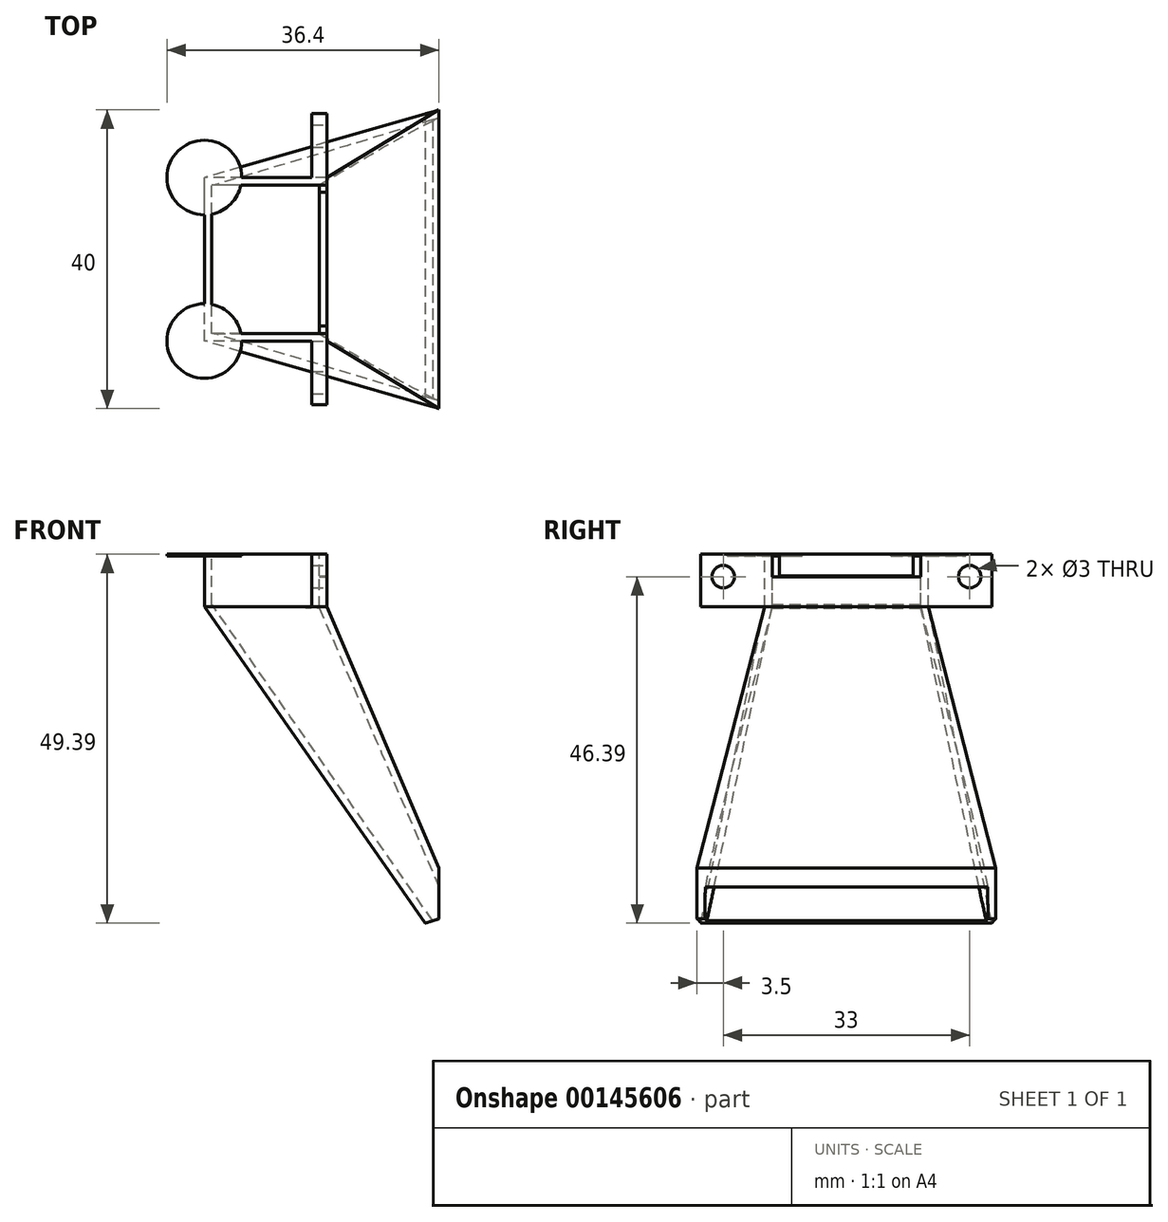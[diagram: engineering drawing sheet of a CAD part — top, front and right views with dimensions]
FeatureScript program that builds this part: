
annotation { "Feature Type Name" : "Feature", "Feature Type Description" : "" }
export const myFeature = defineFeature(function(context is Context, id is Id, definition is map)
    precondition{}
    {
        {
            assignVariable(context, id + "F0", {"name" : "fan_wide", "anyValue" : 19.9});
        }
        {
            assignVariable(context, id + "F1", {"name" : "shell", "anyValue" : 1});
        }
        {
            var Q0;
            Q0=qCreatedBy(makeId("Front.planeOp"),FACE);
            var sketch = newSketch(context, id + "F2", { "sketchPlane" : qUnion([Q0])});
            skLineSegment(sketch, "E0.bottom", {"start": v(0, 0) * mm, "end": v(-16.4, 0) * mm});
            skLineSegment(sketch, "E0.top", {"start": v(0, 7) * mm, "end": v(-16.4, 7) * mm});
            skLineSegment(sketch, "E0.left", {"start": v(0, 0) * mm, "end": v(0, 7) * mm});
            skLineSegment(sketch, "E0.right", {"start": v(-16.4, 0) * mm, "end": v(-16.4, 7) * mm});
            skLineSegment(sketch, "E1", {"start": v(-16.4, 0) * mm, "end": v(15, -45) * mm});
            skLineSegment(sketch, "E2", {"start": v(15, -45) * mm, "end": v(15, -35) * mm});
            skLineSegment(sketch, "E3", {"start": v(15, -35) * mm, "end": v(0, 0) * mm});
            skSolve(sketch);
        }
        {
            var Q0;
            Q0=makeQuery(id+"F2.imprint","IMPRINT",FACE,{"disambiguationData":[TD([[makeQuery(id+"F2.imprint","IMPRINT",EDGE,{"derivedFrom":sQuery(id+"F2.wireOp",EDGE,"E0.bottom")}),-1.0]])]});
            var Q1;
            Q1=makeQuery(id+"F2.imprint","IMPRINT",FACE,{"disambiguationData":[TD([[makeQuery(id+"F2.imprint","IMPRINT",EDGE,{"derivedFrom":sQuery(id+"F2.wireOp",EDGE,"E0.bottom")}),1.0]])]});
            extrude(context, id + "F3", {"entities" : qUnion([Q0, Q1]), "depth" : (getVariable(context, 'fan_wide') + 2 * getVariable(context, 'shell')) * mm, "offsetDistance" : 25 * mm});
        }
        {
            var Q0;
            Q0=qCreatedBy(makeId("Top.planeOp"),FACE);
            var sketch = newSketch(context, id + "F4", { "sketchPlane" : qUnion([Q0])});
            skLineSegment(sketch, "E4.0.0", {"start": v(0, 0) * mm, "end": v(-16.4, 0) * mm});
            skLineSegment(sketch, "E4.0.1", {"start": v(-16.4, 0) * mm, "end": v(-16.4, -21.9) * mm});
            skLineSegment(sketch, "E4.0.2", {"start": v(-16.4, -21.9) * mm, "end": v(0, -21.9) * mm});
            skLineSegment(sketch, "E4.0.3", {"start": v(0, -21.9) * mm, "end": v(0, 0) * mm});
            skSolve(sketch);
        }
        {
            var Q0;
            Q0=makeQuery(id+"F3.opExtrude","SWEPT_FACE",FACE,{"disambiguationData":[OSD([sQuery(id+"F2.wireOp",EDGE,"E2")])]});
            cPlane(context, id + "F5", {"entities" : qUnion([Q0]), "cplaneType" : CPlaneType.OFFSET, "offset" : 0 * mm, "width" : 150 * mm, "height" : 150 * mm});
        }
        {
            var Q0;
            Q0=qCreatedBy(id+"F5.planeOp",FACE);
            var sketch = newSketch(context, id + "F6", { "sketchPlane" : qUnion([Q0])});
            skLineSegment(sketch, "E5.0.0", {"start": v(0, -45) * mm, "end": v(0, -35) * mm, "construction": true});
            skLineSegment(sketch, "E5.0.1", {"start": v(0, -35) * mm, "end": v(-21.9, -35) * mm, "construction": true});
            skLineSegment(sketch, "E5.0.2", {"start": v(-21.9, -35) * mm, "end": v(-21.9, -45) * mm, "construction": true});
            skLineSegment(sketch, "E5.0.3", {"start": v(-21.9, -45) * mm, "end": v(0, -45) * mm, "construction": true});
            skLineSegment(sketch, "E6", {"start": v(-21.9, -35) * mm, "end": v(0, -45) * mm, "construction": true});
            skPoint(sketch, "E7", {"position": v(-10.95, -40) * mm});
            skLineSegment(sketch, "E8.bottom", {"start": v(9.05, -35) * mm, "end": v(-30.95, -35) * mm});
            skLineSegment(sketch, "E8.top", {"start": v(9.05, -45) * mm, "end": v(-30.95, -45) * mm});
            skLineSegment(sketch, "E8.left", {"start": v(9.05, -35) * mm, "end": v(9.05, -45) * mm});
            skLineSegment(sketch, "E8.right", {"start": v(-30.95, -35) * mm, "end": v(-30.95, -45) * mm});
            skSolve(sketch);
        }
        {
            var Q1;
            Q1=makeQuery(id+"F6.imprint","IMPRINT",FACE,{"disambiguationData":[TD([[makeQuery(id+"F6.imprint","IMPRINT",EDGE,{"derivedFrom":sQuery(id+"F6.wireOp",EDGE,"E8.bottom")}),1.0]])]});
            var Q2;
            Q2=makeQuery(id+"F4.imprint","IMPRINT",FACE,{"disambiguationData":[TD([[makeQuery(id+"F4.imprint","IMPRINT",EDGE,{"derivedFrom":sQuery(id+"F4.wireOp",EDGE,"E4.0.0")}),1.0]])]});
            loft(context, id + "F7", {"operationType" : NewBodyOperationType.ADD, "sheetProfilesArray" : [{ "sheetProfileEntities" : qUnion([Q1]) }, { "sheetProfileEntities" : qUnion([Q2]) }]});
        }
        {
            var Q0;
            Q0=makeQuery(id+"F3.opExtrude","SWEPT_FACE",FACE,{"disambiguationData":[OSD([sQuery(id+"F2.wireOp",EDGE,"E0.top")])]});
            var Q1;
            Q1=makeQuery(id+"F7.boolean.opBoolean","MERGE",FACE,{"derivedFrom":[makeQuery(id+"F3.opExtrude","SWEPT_FACE",FACE,{"disambiguationData":[OSD([sQuery(id+"F2.wireOp",EDGE,"E2")])]}),makeQuery(id+"F7.opLoft","CAP_FACE",FACE,{"disambiguationData":[OSD([makeQuery(id+"F6.imprint","IMPRINT",FACE,{"disambiguationData":[TD([[makeQuery(id+"F6.imprint","IMPRINT",EDGE,{"derivedFrom":sQuery(id+"F6.wireOp",EDGE,"E8.bottom")}),1.0]])]})])],"isStart":true})]});
            shell(context, id + "F8", {"entities" : qUnion([Q0, Q1]), "thickness" : (getVariable(context, 'shell')) * mm});
        }
        {
            var Q0;
            Q0=makeQuery(id+"F3.opExtrude","SWEPT_FACE",FACE,{"disambiguationData":[OSD([sQuery(id+"F2.wireOp",EDGE,"E0.left")])]});
            var sketch = newSketch(context, id + "F9", { "sketchPlane" : qUnion([Q0])});
            skLineSegment(sketch, "E9", {"start": v(-10.95, 7) * mm, "end": v(-10.95, 0) * mm, "construction": true});
            skLineSegment(sketch, "E10", {"start": v(-27.45, 4) * mm, "end": v(5.55, 4) * mm, "construction": true});
            skCircle(sketch, "E11", {"center": v(-27.45, 4) * mm, "radius": 1.5 * mm});
            skCircle(sketch, "E12", {"center": v(5.55, 4) * mm, "radius": 1.5 * mm});
            skLineSegment(sketch, "E13.bottom", {"start": v(8.55, 0) * mm, "end": v(-30.45, 0) * mm});
            skLineSegment(sketch, "E13.top", {"start": v(8.55, 7) * mm, "end": v(-30.45, 7) * mm});
            skLineSegment(sketch, "E13.left", {"start": v(8.55, 0) * mm, "end": v(8.55, 7) * mm});
            skLineSegment(sketch, "E13.right", {"start": v(-30.45, 0) * mm, "end": v(-30.45, 7) * mm});
            skPoint(sketch, "E13.middle", {"position": v(-10.95, 3.5) * mm});
            skLineSegment(sketch, "E14.0", {"start": v(-20.9, -0.13) * mm, "end": v(-20.9, 7) * mm, "construction": true});
            skLineSegment(sketch, "E14.1", {"start": v(-1, -0.13) * mm, "end": v(-1, 7) * mm, "construction": true});
            skLineSegment(sketch, "E15.bottom", {"start": v(-20.9, 7) * mm, "end": v(-1, 7) * mm});
            skLineSegment(sketch, "E15.top", {"start": v(-20.9, 4) * mm, "end": v(-1, 4) * mm});
            skLineSegment(sketch, "E15.left", {"start": v(-20.9, 7) * mm, "end": v(-20.9, 4) * mm});
            skLineSegment(sketch, "E15.right", {"start": v(-1, 7) * mm, "end": v(-1, 4) * mm});
            skLineSegment(sketch, "E16.bottom", {"start": v(-19.9, 7) * mm, "end": v(-2, 7) * mm});
            skLineSegment(sketch, "E16.top", {"start": v(-19.9, 4.1) * mm, "end": v(-2, 4.1) * mm});
            skLineSegment(sketch, "E16.left", {"start": v(-19.9, 7) * mm, "end": v(-19.9, 4.1) * mm});
            skLineSegment(sketch, "E16.right", {"start": v(-2, 7) * mm, "end": v(-2, 4.1) * mm});
            skSolve(sketch);
        }
        {
            var Q0;
            Q0=makeQuery(id+"F9.imprint","IMPRINT",FACE,{"disambiguationData":[TD([[makeQuery(id+"F9.imprint","IMPRINT",EDGE,{"derivedFrom":sQuery(id+"F9.wireOp",EDGE,"E12")}),-1.0]])]});
            var Q1;
            Q1=makeQuery(id+"F9.imprint","IMPRINT",FACE,{"disambiguationData":[TD([[makeQuery(id+"F9.imprint","IMPRINT",EDGE,{"derivedFrom":sQuery(id+"F9.wireOp",EDGE,"E11")}),-1.0]])]});
            extrude(context, id + "F10", {"entities" : qUnion([Q0, Q1]), "operationType" : NewBodyOperationType.ADD, "oppositeDirection" : true, "depth" : 2 * mm, "offsetDistance" : 25 * mm});
        }
        {
            var Q0;
            Q0=makeQuery(id+"F9.imprint","IMPRINT",FACE,{"disambiguationData":[TD([[makeQuery(id+"F9.imprint","IMPRINT",EDGE,{"derivedFrom":sQuery(id+"F9.wireOp",EDGE,"E15.top")}),1.0]])]});
            var Q1;
            Q1=makeQuery(id+"F9.imprint","IMPRINT",FACE,{"disambiguationData":[TD([[makeQuery(id+"F9.imprint","IMPRINT",EDGE,{"derivedFrom":sQuery(id+"F9.wireOp",EDGE,"E16.bottom")}),-1.0]])]});
            extrude(context, id + "F11", {"entities" : qUnion([Q0, Q1]), "operationType" : NewBodyOperationType.REMOVE, "oppositeDirection" : true, "depth" : 2 * mm, "offsetDistance" : 25 * mm});
        }
        {
            var Q0;
            Q0=makeQuery(id+"F7.boolean.opBoolean","MERGE",EDGE,{"derivedFrom":[makeQuery(id+"F3.opExtrude","SWEPT_EDGE",EDGE,{"disambiguationData":[OSD([sQuery(id+"F2.wireOp",EDGE,"E1"),sQuery(id+"F2.wireOp",EDGE,"E2")])]}),makeQuery(id+"F7.opLoft","MID_CAP_EDGE",EDGE,{"disambiguationData":[OSD([sQuery(id+"F6.wireOp",EDGE,"E8.top"),sQuery(id+"F6.wireOp",EDGE,"E8.left"),sQuery(id+"F6.wireOp",EDGE,"E8.right")])],"capPos":0.0})]});
            chamfer(context, id + "F12", {"entities" : qUnion([Q0]), "width" : 1 * mm, "tangentPropagation" : true});
        }
        {
            var Q0;
            {var subQ0=sQuery(id+"F9.wireOp",EDGE,"E13.top");Q0=makeQuery(id+"F10.boolean.opBoolean","MERGE",FACE,{"derivedFrom":[makeQuery(id+"F3.opExtrude","SWEPT_FACE",FACE,{"disambiguationData":[OSD([sQuery(id+"F2.wireOp",EDGE,"E0.top")])]}),makeQuery(id+"F10.opExtrude","SWEPT_FACE",FACE,{"disambiguationData":[OSD([subQ0]),TDD([makeQuery(id+"F9.imprint","IMPRINT",EDGE,{"disambiguationData":[TD([[makeQuery(id+"F9.imprint","INTERSECT",VERTEX,{"derivedFrom":[subQ0,sQuery(id+"F9.wireOp",EDGE,"E13.left")]}),-1.0]])],"derivedFrom":subQ0})])]}),makeQuery(id+"F10.opExtrude","SWEPT_FACE",FACE,{"disambiguationData":[OSD([subQ0]),TDD([makeQuery(id+"F9.imprint","IMPRINT",EDGE,{"disambiguationData":[TD([[makeQuery(id+"F9.imprint","INTERSECT",VERTEX,{"derivedFrom":[subQ0,sQuery(id+"F9.wireOp",EDGE,"E13.right")]}),1.0]])],"derivedFrom":subQ0})])]})]});}
            var sketch = newSketch(context, id + "F13", { "sketchPlane" : qUnion([Q0])});
            skCircle(sketch, "E17", {"center": v(-16.4, -21.9) * mm, "radius": 5 * mm});
            skCircle(sketch, "E18", {"center": v(-16.4, 0) * mm, "radius": 5 * mm});
            skSolve(sketch);
        }
        {
            var Q0;
            {var subQ0=sQuery(id+"F13.wireOp",EDGE,"E17");var subQ1=sQuery(id+"F2.wireOp",EDGE,"E0.top");var subQ2=makeQuery(id+"F3.opExtrude","CAP_EDGE",EDGE,{"disambiguationData":[OSD([subQ1])],"isStart":false});var subQ3=makeQuery(id+"F13.imprint","INTERSECT",VERTEX,{"derivedFrom":[subQ2,subQ0]});Q0=makeQuery(id+"F13.imprint","IMPRINT",FACE,{"disambiguationData":[TD([[makeQuery(id+"F13.imprint","IMPRINT",EDGE,{"disambiguationData":[TD([[subQ3,1.0]])],"derivedFrom":subQ0}),1.0]])]});}
            var Q1;
            {var subQ0=sQuery(id+"F13.wireOp",EDGE,"E18");var subQ1=sQuery(id+"F2.wireOp",EDGE,"E0.top");var subQ4=makeQuery(id+"F3.opExtrude","CAP_EDGE",EDGE,{"disambiguationData":[OSD([subQ1])],"isStart":true});var subQ5=makeQuery(id+"F13.imprint","INTERSECT",VERTEX,{"derivedFrom":[subQ4,subQ0]});Q1=makeQuery(id+"F13.imprint","IMPRINT",FACE,{"disambiguationData":[TD([[makeQuery(id+"F13.imprint","IMPRINT",EDGE,{"disambiguationData":[TD([[subQ5,-1.0]])],"derivedFrom":subQ0}),1.0]])]});}
            extrude(context, id + "F14", {"entities" : qUnion([Q0, Q1]), "operationType" : NewBodyOperationType.ADD, "oppositeDirection" : true, "depth" : .2 * mm, "offsetDistance" : 25 * mm});
        }
    });
